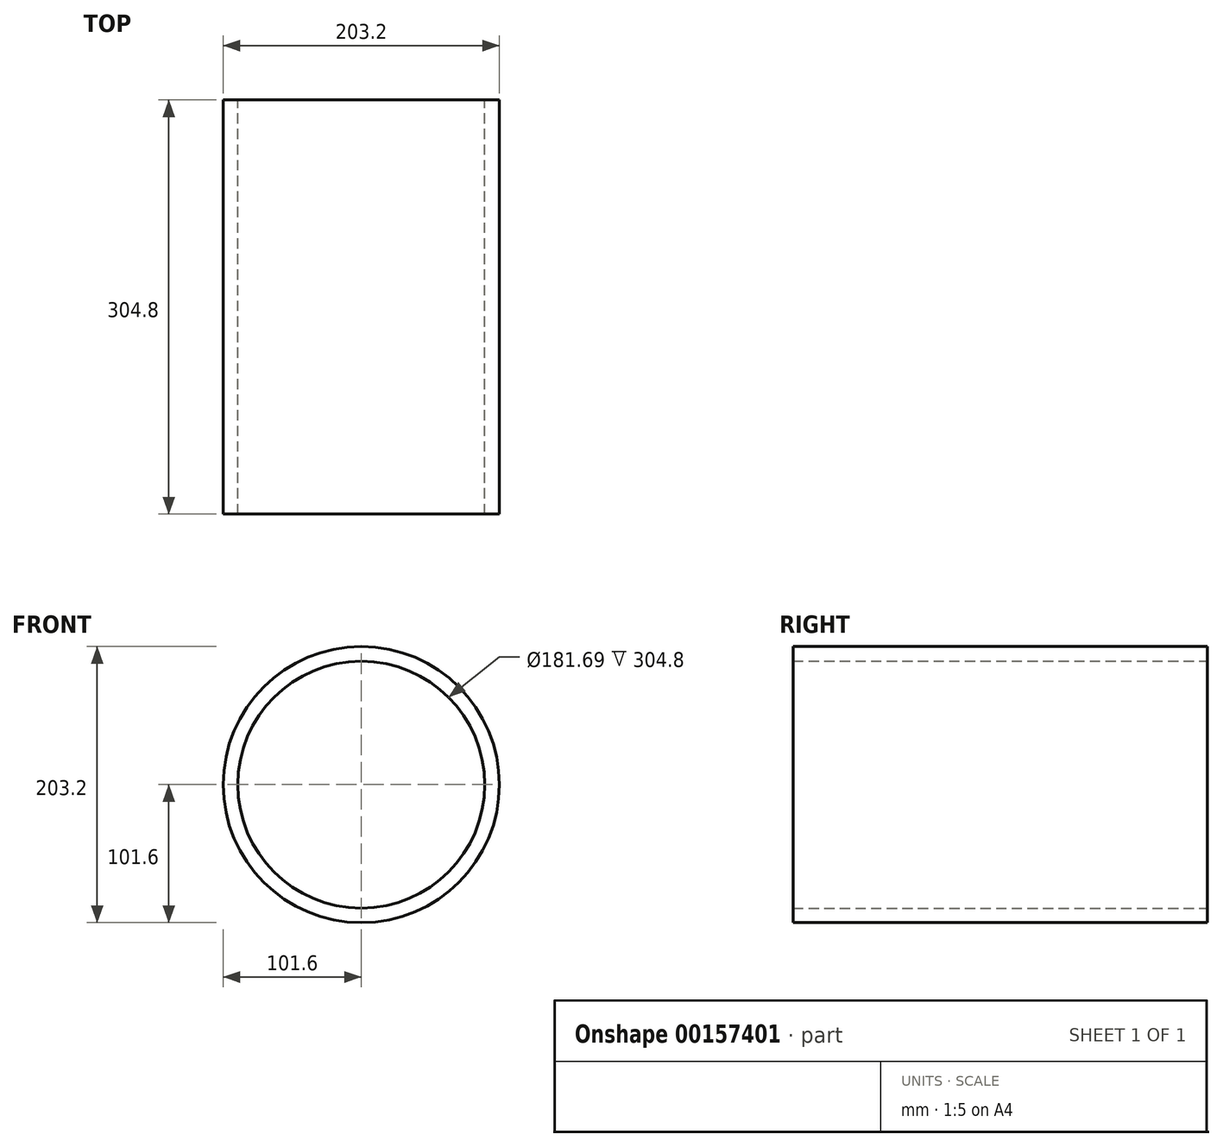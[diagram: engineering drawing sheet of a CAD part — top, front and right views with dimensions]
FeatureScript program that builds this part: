
annotation { "Feature Type Name" : "Feature", "Feature Type Description" : "" }
export const myFeature = defineFeature(function(context is Context, id is Id, definition is map)
    precondition{}
    {
        {
            var Q0;
            Q0=qCreatedBy(makeId("Front.planeOp"),FACE);
            var sketch = newSketch(context, id + "F0", { "sketchPlane" : qUnion([Q0])});
            skCircle(sketch, "E0", {"center": v(0, 0) * mm, "radius": 101.6 * mm});
            skCircle(sketch, "E1", {"center": v(0, 0) * mm, "radius": 90.85 * mm});
            skSolve(sketch);
        }
        {
            var Q0;
            Q0 = qSketchRegion(id + "F0", true);
            extrude(context, id + "F1", {"entities" : qUnion([Q0]), "depth" : 304.8 * mm});
        }
    });
